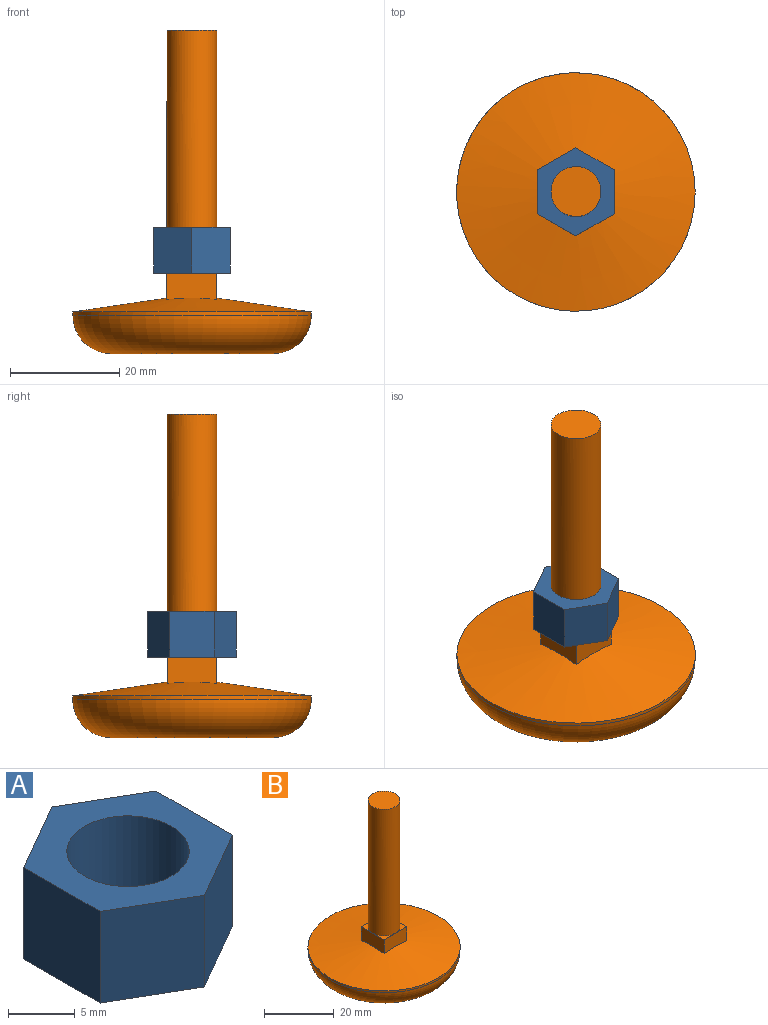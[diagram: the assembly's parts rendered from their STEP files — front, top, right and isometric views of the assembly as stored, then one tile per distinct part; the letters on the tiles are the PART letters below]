
ASSEMBLY  parts=2 mates=1
PART A: 9 faces, bbox 14x16.1x8.4 mm
  f0: plane 8.38x8.07mm, normal (1,0,0), area 67.6mm2, adj f1,f5,f7,f8
  f1: plane 8.38x6.99mm, normal (0.5,0.87,0), area 67.6mm2, adj f0,f2,f7,f8
  f2: plane 8.38x6.99mm, normal (-0.5,0.87,0), area 67.6mm2, adj f1,f3,f7,f8
  f3: plane 8.38x8.07mm, normal (-1,0,0), area 67.6mm2, adj f2,f4,f7,f8
  f4: plane 8.38x6.99mm, normal (-0.5,-0.87,0), area 67.6mm2, adj f3,f5,f7,f8
  f5: plane 8.38x6.99mm, normal (0.5,-0.87,0), area 67.6mm2, adj f0,f4,f7,f8
  f6: cylinder r=4.57mm len=9.14mm, axis (0,0,-1), area 240.8mm2, adj f7,f8
  f7: plane 16.13x13.97mm, normal (0,0,1), area 103.3mm2, adj f0,f1,f2,f3,f4,f5,f6
  f8: plane 16.13x13.97mm, normal (0,0,-1), area 103.3mm2, adj f0,f1,f2,f3,f4,f5,f6
PART B: 14 faces, bbox 47.3x47.3x59.2 mm
  f0: plane 4.57x4.57mm, normal (0,0,1), area 4.5mm2, adj f8,f9,f12
  f1: plane 4.57x4.57mm, normal (0,0,1), area 4.5mm2, adj f9,f10,f12
  f2: plane 4.57x4.57mm, normal (0,0,1), area 4.5mm2, adj f7,f10,f12
  f3: cone r=4.57mm half-angle=81.6deg, axis (0,0,-1), area 1430.7mm2, adj f5,f7,f8,f9,f10
  f4: plane 29.72x29.72mm, normal (0,0,-1), area 693.6mm2, adj f6
  f5: cylinder r=21.84mm len=43.69mm, axis (0,0,1), area 87.2mm2, adj f3,f6
  f6: torus R=14.86mm, axis (0,0,1), area 1330.9mm2, adj f4,f5
  f7: plane 9.15x4.85mm, normal (0,-1,0), area 42.7mm2, adj f2,f3,f8,f10,f11
  f8: plane 9.15x4.85mm, normal (1,0,0), area 42.7mm2, adj f0,f3,f7,f9,f11
  f9: plane 9.15x4.85mm, normal (0,1,0), area 42.7mm2, adj f0,f1,f3,f8,f10
  f10: plane 9.15x4.85mm, normal (-1,0,0), area 42.7mm2, adj f1,f2,f3,f7,f9
  f11: plane 4.57x4.57mm, normal (0,0,1), area 4.5mm2, adj f7,f8,f12
  f12: cylinder r=4.57mm len=44.45mm, axis (0,0,-1), area 1276.9mm2, adj f0,f1,f2,f11,f13
  f13: plane 9.14x9.14mm, normal (0,0,1), area 65.7mm2, adj f12
PLACE A t=(0.06,-0.11,-64.1)mm
PLACE B t=(0.06,-0.11,-19.65)mm fixed
MATE fastened A.f6 <-> B.f12  axis (0,0,-1) through (0.06,-0.11,-15.08)mm
